# Revit family: CA1035551_Grifería para Lavamanos Monocontrol Cascade Media
name_source: partatom
category: Plumbing Fixtures
units: mm (PartAtom-declared; Revit-internal decimal feet)

## family parameters
Always vertical = Yes
Cut with Voids When Loaded = Yes
OmniClass Number = 23.21.21.19
OmniClass Title = Commercial Dishwasher Equipment
Part Type = Normal
Room Calculation Point = No
Round Connector Dimension = Use Diameter
Shared = No
Work Plane-Based = No

## types (1)
- CA1035551_Grifería para Lavamanos Monocontrol Cascade Media
    Acabado = Cromado
    Alto = 23.2 cm
    Altura de la grifería = Media
    Capacidad de flujo = 5.70 l/m máximo a 60 psi
    Colección = Cascade
    Consumo de agua = 5.7 lt
    Creado por = IDD
    Description = La línea de griferías y accesorios Cascade cuenta con líneas fluidas crean un solo viaje alrededor del producto generando formas limpias y un acabado perfecto que resalta la precisión del diseño. Ideal para tu ambiente.
    Fecha de creación = 23/07/2020
    Garantía = 30 años en estructura
    Garantías de otros componentes = 5 años en acabados
    Incluye = Cuerpo, manija
    Largo = 16.4 cm
    Línea = Cascade
    Material = Corona_Plastico_Cromado
    Materiales = Polimero de alta ingenieria
    Premios = A’Design Award
    Productos compatibles = Lavamanos de mesón integrado, Lavamanos para sobreponer, Lavamanos para incrustar, Lavamanos de pedestal, Lavamanos de semipedestal, Lavamanos de colgar
    Rango de presión de agua = Entre 20 y 125 psi
    Resistencia = Resistente a la corrosión pelado y decoloración por agua
    Sistema de accionamiento = Palanca
    Tecnologías = DuraCrome, EcoStream, ThermoControl
    Temperatura de uso = Entre 5˚C y 71˚C
    Tipo de chorro = Espumoso
    Tipo de grifería = Monocontrol
    Tipo de manija/accionamiento = Palanca
    URL = https://corona.co
    Uso = Residencial

## geometry (parser evidence)
native form markers: Sweep x5
no freeform markers — native parametric forms only
